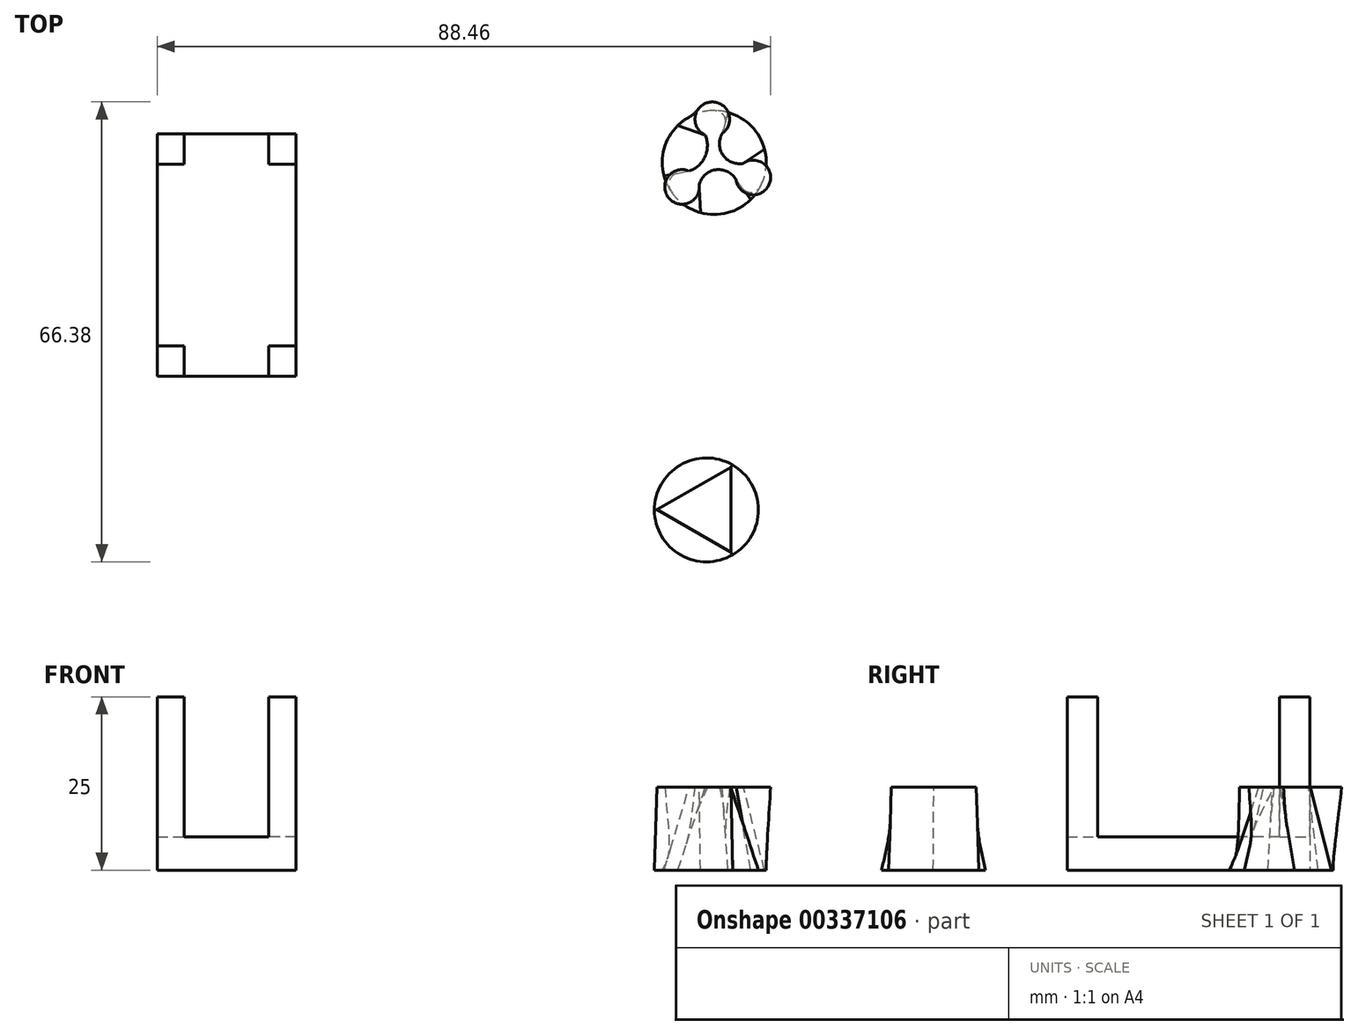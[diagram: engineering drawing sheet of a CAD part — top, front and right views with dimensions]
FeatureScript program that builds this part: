
annotation { "Feature Type Name" : "Feature", "Feature Type Description" : "" }
export const myFeature = defineFeature(function(context is Context, id is Id, definition is map)
    precondition{}
    {
        {
            var Q0;
            Q0=qCreatedBy(makeId("Top.planeOp"),FACE);
            var sketch = newSketch(context, id + "F0", { "sketchPlane" : qUnion([Q0])});
            skLineSegment(sketch, "E0.bottom", {"start": v(-44.5, 40.24) * mm, "end": v(-24.5, 40.24) * mm});
            skLineSegment(sketch, "E0.top", {"start": v(-44.5, 5.24) * mm, "end": v(-24.5, 5.24) * mm});
            skLineSegment(sketch, "E0.left", {"start": v(-44.5, 40.24) * mm, "end": v(-44.5, 5.24) * mm});
            skLineSegment(sketch, "E0.right", {"start": v(-24.5, 40.24) * mm, "end": v(-24.5, 5.24) * mm});
            skSolve(sketch);
        }
        {
            var Q0;
            Q0 = qSketchRegion(id + "F0", true);
            extrude(context, id + "F1", {"entities" : qUnion([Q0]), "depth" : 25 * mm, "offsetDistance" : 25 * mm});
        }
        {
            var Q0;
            Q0=qCreatedBy(makeId("Top.planeOp"),FACE);
            var sketch = newSketch(context, id + "F2", { "sketchPlane" : qUnion([Q0])});
            skLineSegment(sketch, "E1", {"start": v(-28.43, 40.27) * mm, "end": v(-40.6, 40.27) * mm});
            skLineSegment(sketch, "E2", {"start": v(-28.43, 5.26) * mm, "end": v(-28.43, 9.66) * mm});
            skLineSegment(sketch, "E3.MirrorCS", {"start": v(-40.6, 5.26) * mm, "end": v(-40.6, 9.66) * mm});
            skLineSegment(sketch, "E4", {"start": v(-24.5, 35.86) * mm, "end": v(-28.43, 35.86) * mm});
            skLineSegment(sketch, "E5.MirrorCS", {"start": v(-24.5, 9.66) * mm, "end": v(-28.43, 9.66) * mm});
            skLineSegment(sketch, "E6.MirrorCS", {"start": v(-44.54, 35.86) * mm, "end": v(-40.6, 35.86) * mm});
            skLineSegment(sketch, "E7.MirrorCS", {"start": v(-44.54, 9.66) * mm, "end": v(-40.6, 9.66) * mm});
            skPoint(sketch, "E8.start.orphan", {"position": v(-28.43, 22.76) * mm});
            skLineSegment(sketch, "E9.trimOffspring", {"start": v(-28.43, 35.86) * mm, "end": v(-28.43, 40.27) * mm});
            skPoint(sketch, "E10.end.orphan", {"position": v(-34.52, 40.27) * mm});
            skLineSegment(sketch, "E11.trimOffspring", {"start": v(-40.6, 35.86) * mm, "end": v(-40.6, 40.27) * mm});
            skLineSegment(sketch, "E12", {"start": v(-44.52, 35.86) * mm, "end": v(-44.52, 9.66) * mm});
            skPoint(sketch, "E13.orphan", {"position": v(-24.52, 5.26) * mm});
            skPoint(sketch, "E14.orphan", {"position": v(-24.52, 40.27) * mm});
            skPoint(sketch, "E15.orphan", {"position": v(-44.52, 40.27) * mm});
            skLineSegment(sketch, "E16", {"start": v(-24.5, 9.66) * mm, "end": v(-23.09, 9.66) * mm});
            skLineSegment(sketch, "E17", {"start": v(-23.09, 9.66) * mm, "end": v(-23.09, 35.86) * mm});
            skLineSegment(sketch, "E18", {"start": v(-23.09, 35.86) * mm, "end": v(-24.5, 35.86) * mm});
            skLineSegment(sketch, "E19", {"start": v(-28.43, 5.26) * mm, "end": v(-28.43, 1.24) * mm});
            skLineSegment(sketch, "E20", {"start": v(-28.43, 1.24) * mm, "end": v(-40.6, 1.24) * mm});
            skLineSegment(sketch, "E21", {"start": v(-40.6, 1.24) * mm, "end": v(-40.6, 5.26) * mm});
            skSolve(sketch);
        }
        {
            var Q0;
            Q0 = qSketchRegion(id + "F2", true);
            extrude(context, id + "F3", {"entities" : qUnion([Q0]), "operationType" : NewBodyOperationType.REMOVE, "depth" : 27.7 * mm, "offsetDistance" : 25 * mm, "hasSecondDirection" : true, "secondDirectionOppositeDirection" : false, "secondDirectionDepth" : 4.8 * mm});
        }
        {
            var Q0;
            Q0=qCreatedBy(makeId("Top.planeOp"),FACE);
            cPlane(context, id + "F4", {"entities" : qUnion([Q0]), "cplaneType" : CPlaneType.OFFSET, "offset" : 12 * mm, "width" : 150 * mm, "height" : 150 * mm});
        }
        {
            var Q0;
            Q0=qCreatedBy(makeId("Top.planeOp"),FACE);
            var sketch = newSketch(context, id + "F5", { "sketchPlane" : qUnion([Q0])});
            skCircle(sketch, "E22", {"center": v(35.83, 36.12) * mm, "radius": 7.5 * mm});
            skCircle(sketch, "E23", {"center": v(34.7, -14.02) * mm, "radius": 7.5 * mm});
            skSolve(sketch);
        }
        {
            var Q0;
            Q0=qCreatedBy(id+"F4.planeOp",FACE);
            var sketch = newSketch(context, id + "F6", { "sketchPlane" : qUnion([Q0])});
            skArc(sketch, "E24", {"start": v(36.99, 40.32) * mm, "mid": v(35.31, 44.85) * mm, "end": v(34.53, 40.08) * mm});
            skArc(sketch, "E25", {"start": v(38.98, 33.62) * mm, "mid": v(43.75, 32.95) * mm, "end": v(40.02, 36) * mm});
            skArc(sketch, "E26", {"start": v(32.21, 34.88) * mm, "mid": v(29.2, 31.1) * mm, "end": v(33.67, 32.93) * mm});
            skCircle(sketch, "E27.cCircle", {"center": v(34.67, -13.99) * mm, "radius": 3.54 * mm, "construction": true});
            skLineSegment(sketch, "E27.0", {"start": v(38.2, -7.85) * mm, "end": v(38.2, -20.12) * mm});
            skLineSegment(sketch, "E27.1", {"start": v(38.2, -20.12) * mm, "end": v(27.59, -13.99) * mm});
            skLineSegment(sketch, "E27.2", {"start": v(27.59, -13.99) * mm, "end": v(38.2, -7.85) * mm});
            skPoint(sketch, "E27.0.midPoint", {"position": v(38.2, -13.99) * mm});
            skArc(sketch, "E28", {"start": v(32.21, 34.88) * mm, "mid": v(34.51, 36.97) * mm, "end": v(34.53, 40.08) * mm});
            skArc(sketch, "E29", {"start": v(36.99, 40.32) * mm, "mid": v(37.1, 37.17) * mm, "end": v(40.02, 36) * mm});
            skArc(sketch, "E30", {"start": v(38.98, 33.62) * mm, "mid": v(36.1, 35.08) * mm, "end": v(33.67, 32.93) * mm});
            skSolve(sketch);
        }
        {
            var Q0;
            Q0=makeQuery(id+"F5.imprint","IMPRINT",FACE,{"disambiguationData":[TD([[makeQuery(id+"F5.imprint","IMPRINT",EDGE,{"derivedFrom":sQuery(id+"F5.wireOp",EDGE,"E23")}),1.0]])]});
            var Q1;
            Q1=makeQuery(id+"F6.imprint","IMPRINT",FACE,{"disambiguationData":[TD([[makeQuery(id+"F6.imprint","IMPRINT",EDGE,{"derivedFrom":sQuery(id+"F6.wireOp",EDGE,"E27.0")}),-1.0]])]});
            loft(context, id + "F7", {"sheetProfilesArray" : [{ "sheetProfileEntities" : qUnion([Q0]) }, { "sheetProfileEntities" : qUnion([Q1]) }]});
        }
        {
            var Q0;
            Q0=makeQuery(id+"F5.imprint","IMPRINT",FACE,{"disambiguationData":[TD([[makeQuery(id+"F5.imprint","IMPRINT",EDGE,{"derivedFrom":sQuery(id+"F5.wireOp",EDGE,"E22")}),1.0]])]});
            var Q1;
            Q1=makeQuery(id+"F6.imprint","IMPRINT",FACE,{"disambiguationData":[TD([[makeQuery(id+"F6.imprint","IMPRINT",EDGE,{"derivedFrom":sQuery(id+"F6.wireOp",EDGE,"E24")}),1.0]])]});
            loft(context, id + "F8", {"sheetProfilesArray" : [{ "sheetProfileEntities" : qUnion([Q0]) }, { "sheetProfileEntities" : qUnion([Q1]) }]});
        }
    });
